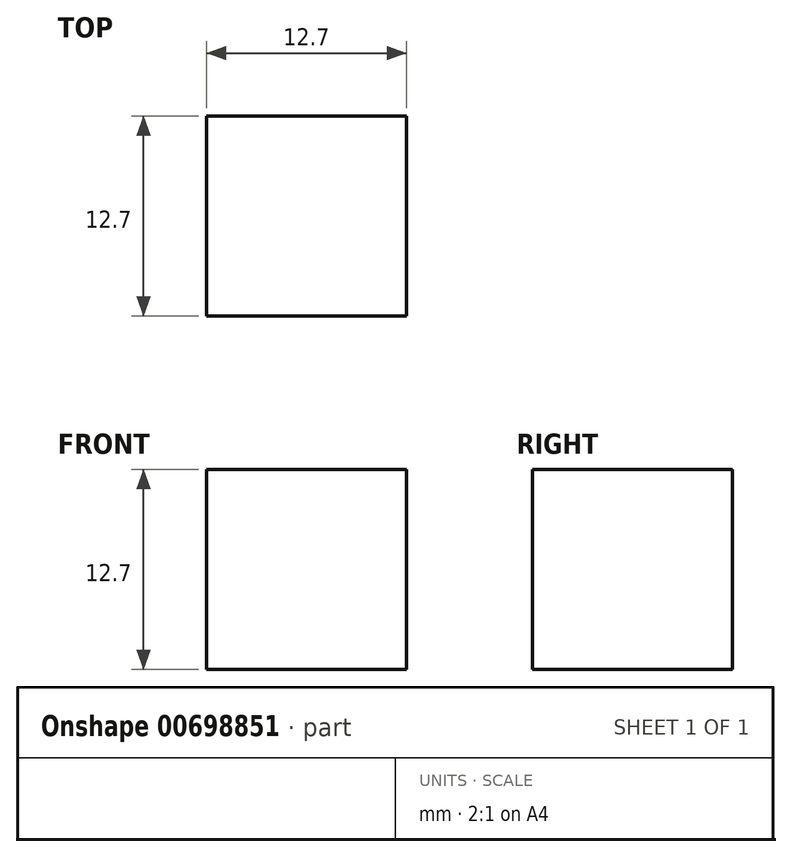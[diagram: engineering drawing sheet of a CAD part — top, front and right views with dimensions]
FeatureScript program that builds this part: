
annotation { "Feature Type Name" : "Feature", "Feature Type Description" : "" }
export const myFeature = defineFeature(function(context is Context, id is Id, definition is map)
    precondition{}
    {
        {
            var Q0;
            Q0=qCreatedBy(makeId("Front.planeOp"),FACE);
            var sketch = newSketch(context, id + "F0", { "sketchPlane" : qUnion([Q0])});
            skLineSegment(sketch, "E0", {"start": v(0, 0) * mm, "end": v(0, 12.7) * mm});
            skLineSegment(sketch, "E1", {"start": v(0, 12.7) * mm, "end": v(-12.7, 12.7) * mm});
            skLineSegment(sketch, "E2", {"start": v(-12.7, 12.7) * mm, "end": v(-12.7, 0) * mm});
            skLineSegment(sketch, "E3", {"start": v(-12.7, 0) * mm, "end": v(0, 0) * mm});
            skSolve(sketch);
        }
        {
            var Q0;
            Q0=makeQuery(id+"F0.imprint","IMPRINT",FACE,{"disambiguationData":[TD([[makeQuery(id+"F0.imprint","IMPRINT",EDGE,{"derivedFrom":sQuery(id+"F0.wireOp",EDGE,"E0")}),1.0]])]});
            extrude(context, id + "F1", {"entities" : qUnion([Q0]), "depth" : 12.7 * mm, "offsetDistance" : 25.4 * mm});
        }
    });
